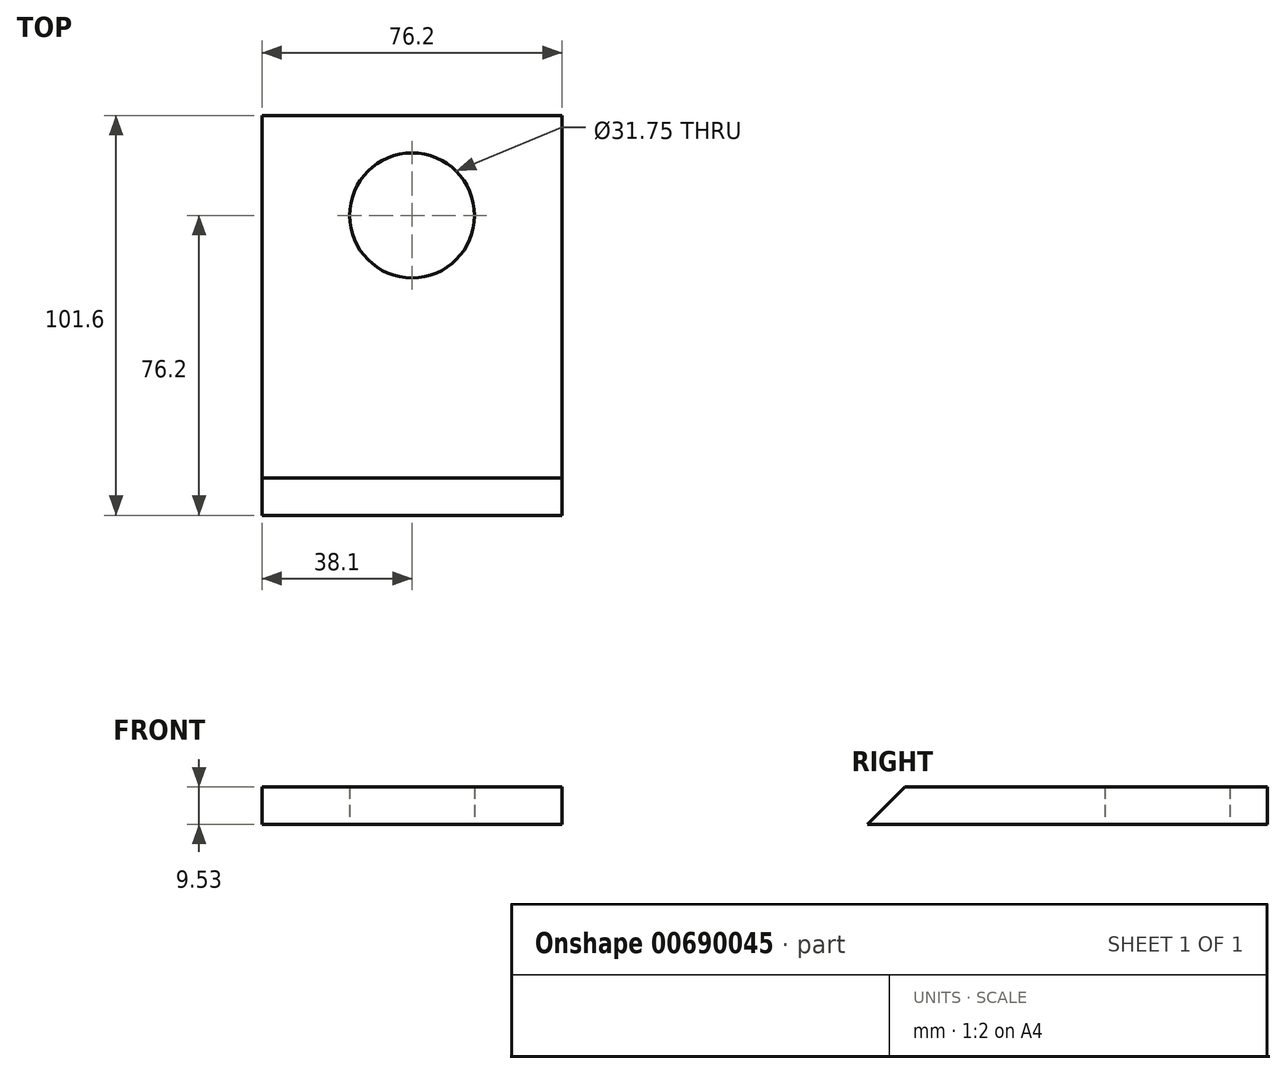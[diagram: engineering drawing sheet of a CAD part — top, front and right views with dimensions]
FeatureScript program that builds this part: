
annotation { "Feature Type Name" : "Feature", "Feature Type Description" : "" }
export const myFeature = defineFeature(function(context is Context, id is Id, definition is map)
    precondition{}
    {
        {
            var Q0;
            Q0=qCreatedBy(makeId("Top.planeOp"),FACE);
            var sketch = newSketch(context, id + "F0", { "sketchPlane" : qUnion([Q0])});
            skLineSegment(sketch, "E0.bottom", {"start": v(-38.1, 50.8) * mm, "end": v(38.1, 50.8) * mm});
            skLineSegment(sketch, "E0.top", {"start": v(-38.1, -50.8) * mm, "end": v(38.1, -50.8) * mm});
            skLineSegment(sketch, "E0.left", {"start": v(-38.1, 50.8) * mm, "end": v(-38.1, -50.8) * mm});
            skLineSegment(sketch, "E0.right", {"start": v(38.1, 50.8) * mm, "end": v(38.1, -50.8) * mm});
            skPoint(sketch, "E0.middle", {"position": v(0, 0) * mm});
            skSolve(sketch);
        }
        {
            var Q0;
            Q0 = qSketchRegion(id + "F0", true);
            extrude(context, id + "F1", {"entities" : qUnion([Q0]), "depth" : 9.52 * mm, "offsetDistance" : 25.4 * mm});
        }
        {
            var Q0;
            Q0=makeQuery(id+"F1.opExtrude","CAP_EDGE",EDGE,{"disambiguationData":[OSD([sQuery(id+"F0.wireOp",EDGE,"E0.top")])],"isStart":false});
            chamfer(context, id + "F2", {"entities" : qUnion([Q0]), "width" : 9.52 * mm, "tangentPropagation" : true});
        }
        {
            var Q0;
            Q0=makeQuery(id+"F1.opExtrude","CAP_FACE",FACE,{"disambiguationData":[OSD([sQuery(id+"F0.wireOp",EDGE,"E0.bottom"),sQuery(id+"F0.wireOp",EDGE,"E0.top"),sQuery(id+"F0.wireOp",EDGE,"E0.left"),sQuery(id+"F0.wireOp",EDGE,"E0.right")])],"isStart":true});
            var sketch = newSketch(context, id + "F3", { "sketchPlane" : qUnion([Q0])});
            skCircle(sketch, "E1", {"center": v(0, -25.4) * mm, "radius": 15.88 * mm});
            skLineSegment(sketch, "E2", {"start": v(0, -50.8) * mm, "end": v(0, -25.4) * mm, "construction": true});
            skSolve(sketch);
        }
        {
            var Q0;
            Q0 = qSketchRegion(id + "F3", true);
            extrude(context, id + "F4", {"entities" : qUnion([Q0]), "operationType" : NewBodyOperationType.REMOVE, "oppositeDirection" : true, "depth" : 9.52 * mm, "offsetDistance" : 25.4 * mm});
        }
    });
